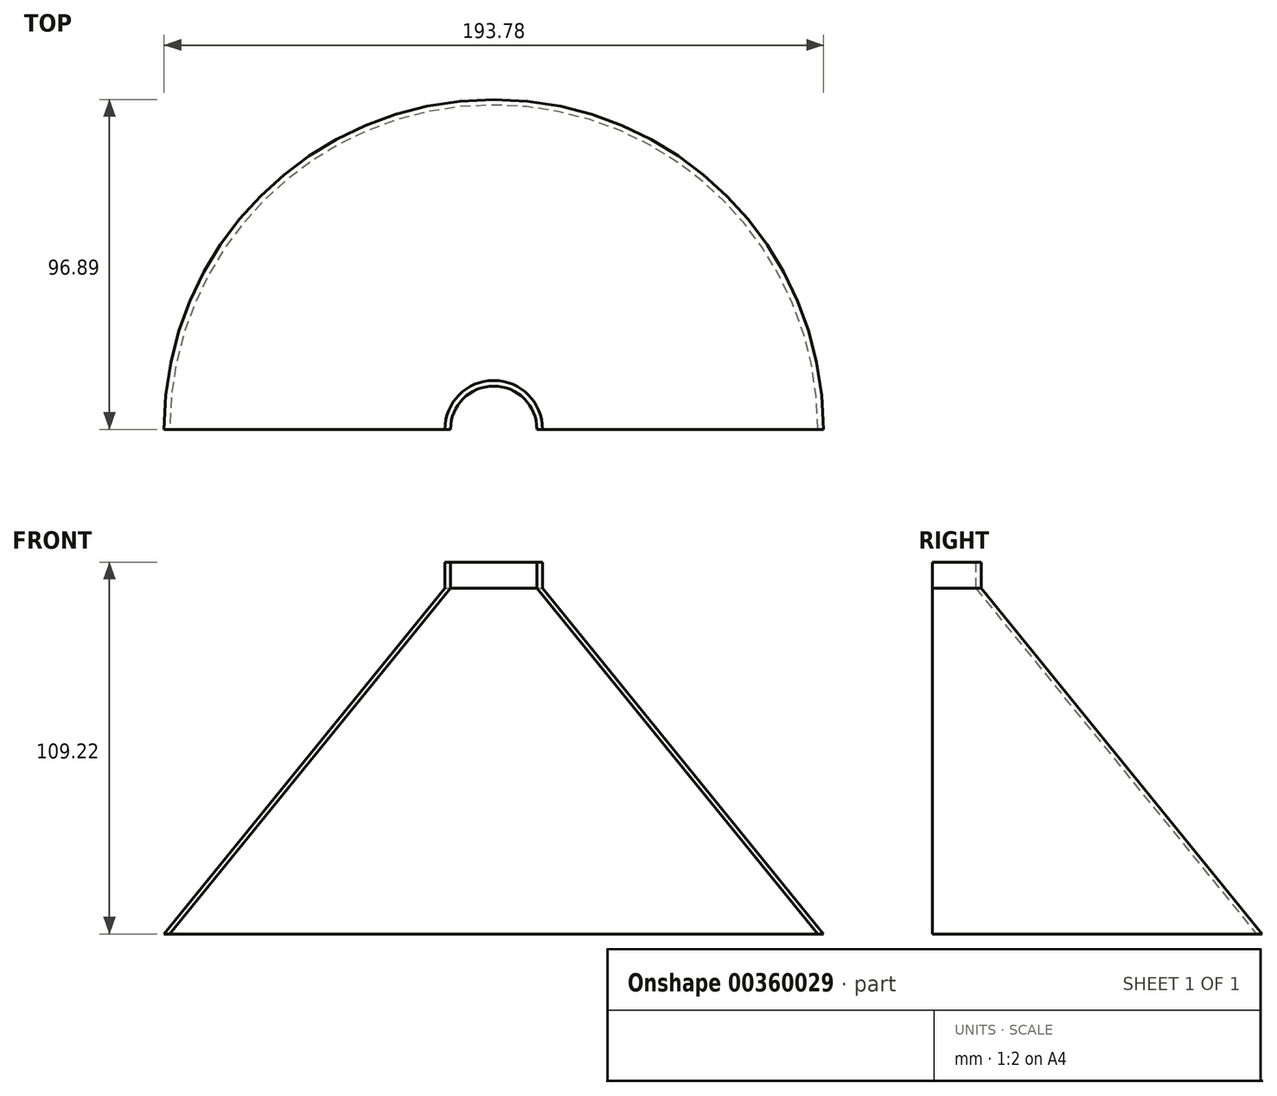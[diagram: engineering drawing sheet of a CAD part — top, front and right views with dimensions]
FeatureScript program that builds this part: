
annotation { "Feature Type Name" : "Feature", "Feature Type Description" : "" }
export const myFeature = defineFeature(function(context is Context, id is Id, definition is map)
    precondition{}
    {
        {
            var Q0;
            Q0=qCreatedBy(makeId("Front.planeOp"),FACE);
            var sketch = newSketch(context, id + "F0", { "sketchPlane" : qUnion([Q0])});
            skLineSegment(sketch, "E0", {"start": v(95.25, 0) * mm, "end": v(12.7, 101.6) * mm});
            skLineSegment(sketch, "E1", {"start": v(12.7, 101.6) * mm, "end": v(14.34, 101.6) * mm});
            skLineSegment(sketch, "E2", {"start": v(14.34, 101.6) * mm, "end": v(96.89, 0) * mm});
            skLineSegment(sketch, "E3", {"start": v(96.89, 0) * mm, "end": v(95.25, 0) * mm});
            skLineSegment(sketch, "E4", {"start": v(12.7, 101.6) * mm, "end": v(12.7, 109.22) * mm});
            skLineSegment(sketch, "E5", {"start": v(12.7, 109.22) * mm, "end": v(14.34, 109.22) * mm});
            skLineSegment(sketch, "E6", {"start": v(14.34, 109.22) * mm, "end": v(14.34, 101.6) * mm});
            skSolve(sketch);
        }
        {
            var Q0;
            Q0=qCreatedBy(makeId("Right.planeOp"),FACE);
            var sketch = newSketch(context, id + "F1", { "sketchPlane" : qUnion([Q0])});
            skLineSegment(sketch, "E7", {"start": v(0, 0) * mm, "end": v(0, 58.57) * mm});
            skSolve(sketch);
        }
        {
            var Q0;
            Q0 = qSketchRegion(id + "F0", true);
            var Q1;
            Q1=sQuery(id+"F1.wireOp",EDGE,"E7");
            revolve(context, id + "F2", {"entities" : qUnion([Q0]), "axis" : qUnion([Q1]), "revolveType" : RevolveType.ONE_DIRECTION, "angle" : 180 * degree});
        }
    });
